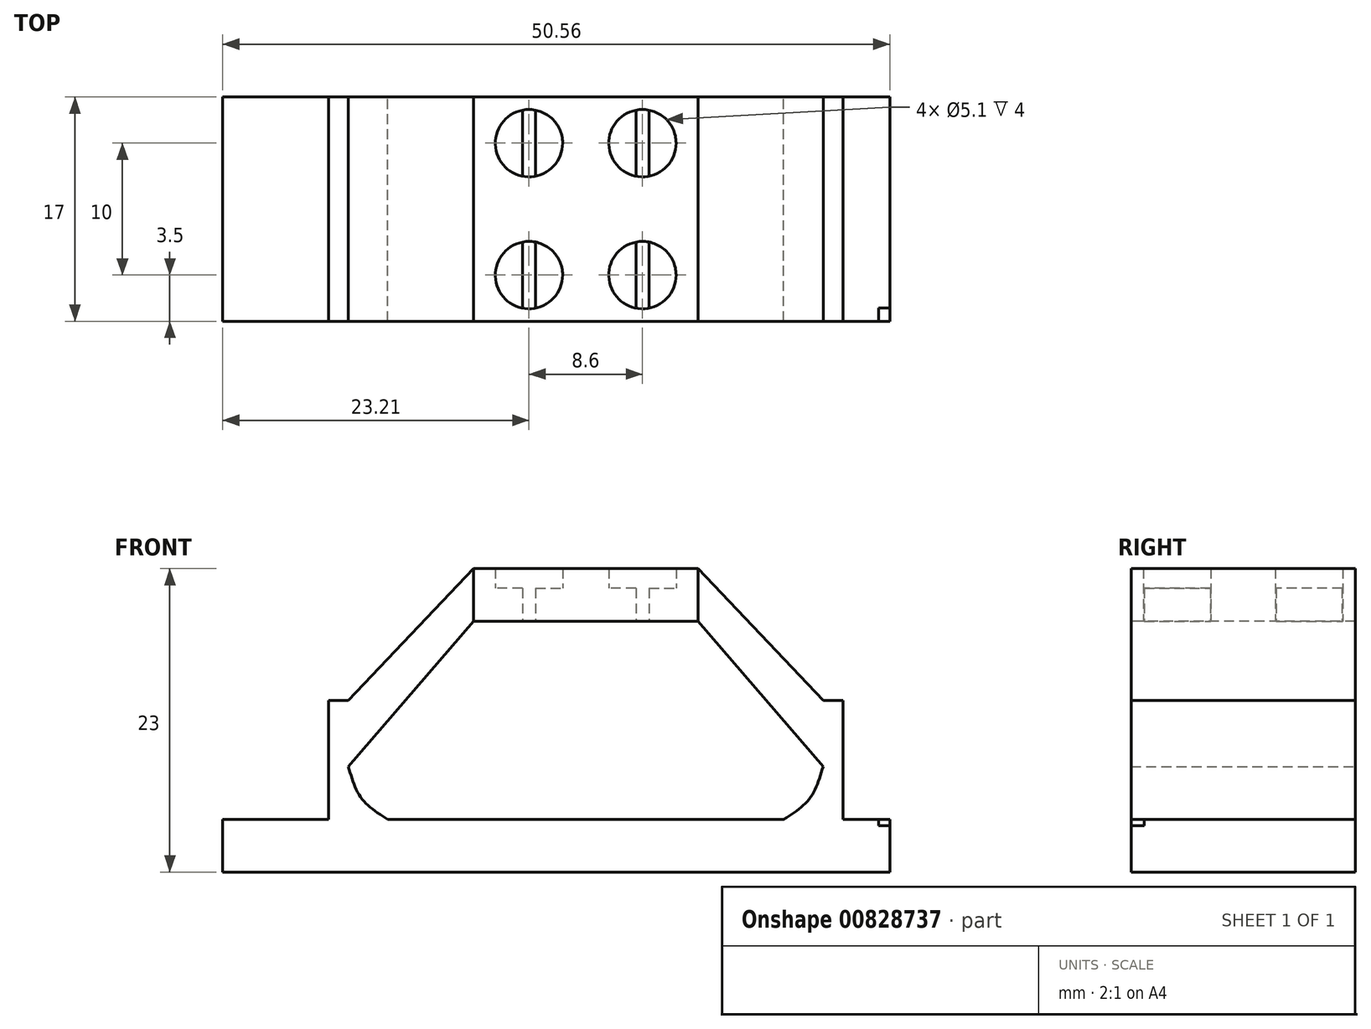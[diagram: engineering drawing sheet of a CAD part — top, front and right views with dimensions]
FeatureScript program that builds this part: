
annotation { "Feature Type Name" : "Feature", "Feature Type Description" : "" }
export const myFeature = defineFeature(function(context is Context, id is Id, definition is map)
    precondition{}
    {
        {
            assignVariable(context, id + "F0", {"name" : "Hollow", "anyValue" : 82});
        }
        {
            assignVariable(context, id + "F1", {"name" : "BaseThicknes", "anyValue" : 4});
        }
        {
            var Q0;
            Q0=qCreatedBy(makeId("Top.planeOp"),FACE);
            cPlane(context, id + "F2", {"entities" : qUnion([Q0]), "cplaneType" : CPlaneType.OFFSET, "offset" : (sqrt((sqrt((getVariable(context, 'Hollow') * getVariable(context, 'Hollow')) - ((getVariable(context, 'Hollow') / 2) * (getVariable(context, 'Hollow') / 2)))) * (sqrt((getVariable(context, 'Hollow') * getVariable(context, 'Hollow')) - ((getVariable(context, 'Hollow') / 2) * (getVariable(context, 'Hollow') / 2)))) - ((getVariable(context, 'Hollow') / 2) * (getVariable(context, 'Hollow') / 2)))) * mm, "width" : 150 * mm, "height" : 150 * mm});
        }
        {
            var Q0;
            Q0=qCreatedBy(id+"F2.planeOp",FACE);
            var sketch = newSketch(context, id + "F3", { "sketchPlane" : qUnion([Q0])});
            skPoint(sketch, "E0", {"position": v(0, 0) * mm});
            skSolve(sketch);
        }
        {
            var Q0;
            Q0=qCreatedBy(makeId("Top.planeOp"),FACE);
            var sketch = newSketch(context, id + "F4", { "sketchPlane" : qUnion([Q0])});
            skLineSegment(sketch, "E1.bottom", {"start": v(-41, 41) * mm, "end": v(41, 41) * mm});
            skLineSegment(sketch, "E1.top", {"start": v(-41, -41) * mm, "end": v(41, -41) * mm});
            skLineSegment(sketch, "E1.left", {"start": v(-41, 41) * mm, "end": v(-41, -41) * mm});
            skLineSegment(sketch, "E1.right", {"start": v(41, 41) * mm, "end": v(41, -41) * mm});
            skSolve(sketch);
        }
        {
            var Q0;
            Q0=qSketchRegion(id+"F4",true);
            extrude(context, id + "F5", {"entities" : qUnion([Q0]), "depth" : (getVariable(context, 'BaseThicknes')) * mm, "offsetDistance" : 25 * mm});
        }
        {
            var Q1;
            Q1=makeQuery(id+"F5.opExtrude","CAP_FACE",FACE,{"disambiguationData":[OSD([sQuery(id+"F4.wireOp",EDGE,"E1.bottom"),sQuery(id+"F4.wireOp",EDGE,"E1.top"),sQuery(id+"F4.wireOp",EDGE,"E1.left"),sQuery(id+"F4.wireOp",EDGE,"E1.right")])],"isStart":true});
            var Q2;
            Q2=sQuery(id+"F3.wireOp",VERTEX,"E0");
            loft(context, id + "F6", {"operationType" : NewBodyOperationType.INTERSECT, "sheetProfilesArray" : [{ "sheetProfileEntities" : qUnion([Q1]) }, { "sheetProfileEntities" : qUnion([Q2]) }]});
        }
        {
            var Q0;
            Q0=makeQuery(id+"F5.opExtrude","CAP_FACE",FACE,{"disambiguationData":[OSD([sQuery(id+"F4.wireOp",EDGE,"E1.bottom"),sQuery(id+"F4.wireOp",EDGE,"E1.top"),sQuery(id+"F4.wireOp",EDGE,"E1.left"),sQuery(id+"F4.wireOp",EDGE,"E1.right")])],"isStart":true});
            var sketch = newSketch(context, id + "F7", { "sketchPlane" : qUnion([Q0])});
            skCircle(sketch, "E2", {"center": v(-34.94, -34.94) * mm, "radius": 0.76 * mm});
            skCircle(sketch, "E3.MirrorC", {"center": v(34.94, -34.94) * mm, "radius": 0.76 * mm});
            skCircle(sketch, "E4.MirrorC", {"center": v(34.94, 34.94) * mm, "radius": 0.76 * mm});
            skCircle(sketch, "E5.MirrorC", {"center": v(-34.94, 34.94) * mm, "radius": 0.76 * mm});
            skCircle(sketch, "E6", {"center": v(-34.94, -34.94) * mm, "radius": 1.51 * mm});
            skCircle(sketch, "E7.MirrorC", {"center": v(-34.94, 34.94) * mm, "radius": 1.51 * mm});
            skCircle(sketch, "E8.MirrorC", {"center": v(34.94, -34.94) * mm, "radius": 1.51 * mm});
            skCircle(sketch, "E9.MirrorC", {"center": v(34.94, 34.94) * mm, "radius": 1.51 * mm});
            skSolve(sketch);
        }
        {
            var Q0;
            Q0=makeQuery(id+"F7.imprint","IMPRINT",FACE,{"disambiguationData":[TD([[makeQuery(id+"F7.imprint","IMPRINT",EDGE,{"derivedFrom":sQuery(id+"F7.wireOp",EDGE,"E2")}),1.0]])]});
            var Q1;
            Q1=makeQuery(id+"F7.imprint","IMPRINT",FACE,{"disambiguationData":[TD([[makeQuery(id+"F7.imprint","IMPRINT",EDGE,{"derivedFrom":sQuery(id+"F7.wireOp",EDGE,"E5.MirrorC")}),-1.0]])]});
            var Q2;
            Q2=makeQuery(id+"F7.imprint","IMPRINT",FACE,{"disambiguationData":[TD([[makeQuery(id+"F7.imprint","IMPRINT",EDGE,{"derivedFrom":sQuery(id+"F7.wireOp",EDGE,"E4.MirrorC")}),1.0]])]});
            var Q3;
            Q3=makeQuery(id+"F7.imprint","IMPRINT",FACE,{"disambiguationData":[TD([[makeQuery(id+"F7.imprint","IMPRINT",EDGE,{"derivedFrom":sQuery(id+"F7.wireOp",EDGE,"E3.MirrorC")}),-1.0]])]});
            extrude(context, id + "F8", {"entities" : qUnion([Q0, Q1, Q2, Q3]), "operationType" : NewBodyOperationType.REMOVE, "oppositeDirection" : true, "depth" : 25 * mm, "offsetDistance" : 25 * mm});
        }
        {
            var Q0;
            Q0=makeQuery(id+"F7.imprint","IMPRINT",FACE,{"disambiguationData":[TD([[makeQuery(id+"F7.imprint","IMPRINT",EDGE,{"derivedFrom":sQuery(id+"F7.wireOp",EDGE,"E5.MirrorC")}),1.0]])]});
            var Q1;
            Q1=makeQuery(id+"F7.imprint","IMPRINT",FACE,{"disambiguationData":[TD([[makeQuery(id+"F7.imprint","IMPRINT",EDGE,{"derivedFrom":sQuery(id+"F7.wireOp",EDGE,"E4.MirrorC")}),-1.0]])]});
            var Q2;
            Q2=makeQuery(id+"F7.imprint","IMPRINT",FACE,{"disambiguationData":[TD([[makeQuery(id+"F7.imprint","IMPRINT",EDGE,{"derivedFrom":sQuery(id+"F7.wireOp",EDGE,"E2")}),-1.0]])]});
            var Q3;
            Q3=makeQuery(id+"F7.imprint","IMPRINT",FACE,{"disambiguationData":[TD([[makeQuery(id+"F7.imprint","IMPRINT",EDGE,{"derivedFrom":sQuery(id+"F7.wireOp",EDGE,"E3.MirrorC")}),1.0]])]});
            extrude(context, id + "F9", {"entities" : qUnion([Q0, Q1, Q2, Q3]), "operationType" : NewBodyOperationType.REMOVE, "oppositeDirection" : true, "depth" : 2 * mm, "offsetDistance" : 25 * mm});
        }
        {
            var Q0;
            Q0=makeQuery(id+"F5.opExtrude","CAP_FACE",FACE,{"disambiguationData":[OSD([sQuery(id+"F4.wireOp",EDGE,"E1.bottom"),sQuery(id+"F4.wireOp",EDGE,"E1.top"),sQuery(id+"F4.wireOp",EDGE,"E1.left"),sQuery(id+"F4.wireOp",EDGE,"E1.right")])],"isStart":false});
            var sketch = newSketch(context, id + "F10", { "sketchPlane" : qUnion([Q0])});
            skLineSegment(sketch, "E10.bottom", {"start": v(-30, 29.5) * mm, "end": v(-26.3, 29.5) * mm});
            skLineSegment(sketch, "E10.top", {"start": v(-30, -16.5) * mm, "end": v(-26.3, -16.5) * mm});
            skLineSegment(sketch, "E10.left", {"start": v(-30, 29.5) * mm, "end": v(-30, -16.5) * mm});
            skLineSegment(sketch, "E10.right", {"start": v(-19.5, 29.5) * mm, "end": v(-19.5, -16.5) * mm});
            skLineSegment(sketch, "E11.bottom", {"start": v(-31.5, 31.5) * mm, "end": v(-26.3, 31.5) * mm});
            skLineSegment(sketch, "E11.top", {"start": v(-31.5, -18.5) * mm, "end": v(-18, -18.5) * mm});
            skLineSegment(sketch, "E11.left", {"start": v(-31.5, 31.5) * mm, "end": v(-31.5, -18.5) * mm});
            skLineSegment(sketch, "E11.right", {"start": v(-18, 31.5) * mm, "end": v(-18, -18.5) * mm});
            skLineSegment(sketch, "E12", {"start": v(-30, 27.7) * mm, "end": v(-28, 27.7) * mm});
            skLineSegment(sketch, "E13", {"start": v(-30, 28.7) * mm, "end": v(-28, 28.7) * mm});
            skLineSegment(sketch, "E14.left", {"start": v(-21.5, 28.7) * mm, "end": v(-21.5, 27.7) * mm});
            skLineSegment(sketch, "E14.right", {"start": v(-28, 28.7) * mm, "end": v(-28, 27.7) * mm});
            skLineSegment(sketch, "E15", {"start": v(-18, 6.5) * mm, "end": v(-31.5, 6.5) * mm, "construction": true});
            skLineSegment(sketch, "E16.trimOffspring", {"start": v(-21.5, 27.7) * mm, "end": v(-19.5, 27.7) * mm});
            skLineSegment(sketch, "E17.trimOffspring", {"start": v(-21.5, 28.7) * mm, "end": v(-19.5, 28.7) * mm});
            skLineSegment(sketch, "E18.MirrorCS", {"start": v(-30, -15.7) * mm, "end": v(-28, -15.7) * mm});
            skLineSegment(sketch, "E19.MirrorCS", {"start": v(-30, -14.7) * mm, "end": v(-28, -14.7) * mm});
            skLineSegment(sketch, "E20.MirrorCS", {"start": v(-21.5, -15.7) * mm, "end": v(-21.5, -14.7) * mm});
            skLineSegment(sketch, "E21.MirrorCS", {"start": v(-21.5, -15.7) * mm, "end": v(-19.5, -15.7) * mm});
            skLineSegment(sketch, "E22.MirrorCS", {"start": v(-21.5, -14.7) * mm, "end": v(-19.5, -14.7) * mm});
            skLineSegment(sketch, "E23.MirrorCS", {"start": v(-28, -15.7) * mm, "end": v(-28, -14.7) * mm});
            skLineSegment(sketch, "E24", {"start": v(-26.3, 31.5) * mm, "end": v(-26.3, 29.5) * mm});
            skLineSegment(sketch, "E25", {"start": v(-23.2, 31.5) * mm, "end": v(-23.2, 29.5) * mm});
            skLineSegment(sketch, "E26.trimOffspring", {"start": v(-23.2, 31.5) * mm, "end": v(-18, 31.5) * mm});
            skLineSegment(sketch, "E27.trimOffspring", {"start": v(-23.2, 29.5) * mm, "end": v(-19.5, 29.5) * mm});
            skLineSegment(sketch, "E28.MirrorCS", {"start": v(-26.3, -18.5) * mm, "end": v(-26.3, -16.5) * mm});
            skLineSegment(sketch, "E29.MirrorCS", {"start": v(-23.2, -18.5) * mm, "end": v(-23.2, -16.5) * mm});
            skLineSegment(sketch, "E30.trimOffspring", {"start": v(-23.2, -16.5) * mm, "end": v(-19.5, -16.5) * mm});
            skLineSegment(sketch, "E31.MirrorCS", {"start": v(21.5, 28.7) * mm, "end": v(21.5, 27.7) * mm});
            skLineSegment(sketch, "E32.MirrorCS", {"start": v(21.5, 28.7) * mm, "end": v(19.5, 28.7) * mm});
            skLineSegment(sketch, "E33.MirrorCS", {"start": v(23.2, 29.5) * mm, "end": v(19.5, 29.5) * mm});
            skLineSegment(sketch, "E34.MirrorCS", {"start": v(23.2, 31.5) * mm, "end": v(23.2, 29.5) * mm});
            skLineSegment(sketch, "E35.MirrorCS", {"start": v(28, -15.7) * mm, "end": v(28, -14.7) * mm});
            skLineSegment(sketch, "E36.MirrorCS", {"start": v(21.5, -15.7) * mm, "end": v(19.5, -15.7) * mm});
            skLineSegment(sketch, "E37.MirrorCS", {"start": v(23.2, -16.5) * mm, "end": v(19.5, -16.5) * mm});
            skLineSegment(sketch, "E38.MirrorCS", {"start": v(30, -15.7) * mm, "end": v(28, -15.7) * mm});
            skLineSegment(sketch, "E39.MirrorCS", {"start": v(21.5, -14.7) * mm, "end": v(19.5, -14.7) * mm});
            skLineSegment(sketch, "E40.MirrorCS", {"start": v(30, 29.5) * mm, "end": v(26.3, 29.5) * mm});
            skLineSegment(sketch, "E41.MirrorCS", {"start": v(30, 28.7) * mm, "end": v(28, 28.7) * mm});
            skLineSegment(sketch, "E42.MirrorCS", {"start": v(30, -16.5) * mm, "end": v(26.3, -16.5) * mm});
            skLineSegment(sketch, "E43.MirrorCS", {"start": v(26.3, 31.5) * mm, "end": v(26.3, 29.5) * mm});
            skLineSegment(sketch, "E44.MirrorCS", {"start": v(21.5, -15.7) * mm, "end": v(21.5, -14.7) * mm});
            skLineSegment(sketch, "E45.MirrorCS", {"start": v(28, 28.7) * mm, "end": v(28, 27.7) * mm});
            skLineSegment(sketch, "E46.MirrorCS", {"start": v(30, -14.7) * mm, "end": v(28, -14.7) * mm});
            skLineSegment(sketch, "E47.MirrorCS", {"start": v(31.5, 31.5) * mm, "end": v(26.3, 31.5) * mm});
            skLineSegment(sketch, "E48.MirrorCS", {"start": v(21.5, 27.7) * mm, "end": v(19.5, 27.7) * mm});
            skLineSegment(sketch, "E49.MirrorCS", {"start": v(23.2, -18.5) * mm, "end": v(23.2, -16.5) * mm});
            skLineSegment(sketch, "E50.MirrorCS", {"start": v(30, 27.7) * mm, "end": v(28, 27.7) * mm});
            skLineSegment(sketch, "E51.MirrorCS", {"start": v(26.3, -18.5) * mm, "end": v(26.3, -16.5) * mm});
            skLineSegment(sketch, "E52.MirrorCS", {"start": v(23.2, 31.5) * mm, "end": v(18, 31.5) * mm});
            skLineSegment(sketch, "E53.MirrorCS", {"start": v(31.5, 31.5) * mm, "end": v(31.5, -18.5) * mm});
            skLineSegment(sketch, "E54.MirrorCS", {"start": v(30, 29.5) * mm, "end": v(30, -16.5) * mm});
            skLineSegment(sketch, "E55.MirrorCS", {"start": v(31.5, -18.5) * mm, "end": v(18, -18.5) * mm});
            skLineSegment(sketch, "E56.MirrorCS", {"start": v(19.5, 29.5) * mm, "end": v(19.5, -16.5) * mm});
            skLineSegment(sketch, "E57.MirrorCS", {"start": v(18, 31.5) * mm, "end": v(18, -18.5) * mm});
            skLineSegment(sketch, "E58.MirrorCS", {"start": v(18, 6.5) * mm, "end": v(31.5, 6.5) * mm, "construction": true});
            skSolve(sketch);
        }
        {
            var Q0;
            {var subQ5=sQuery(id+"F10.wireOp",EDGE,"E33.MirrorCS");Q0=makeQuery(id+"F10.imprint","IMPRINT",FACE,{"disambiguationData":[TD([[makeQuery(id+"F10.imprint","IMPRINT",EDGE,{"derivedFrom":subQ5}),-1.0]])]});}
            var Q1;
            {var subQ6=sQuery(id+"F10.wireOp",EDGE,"E40.MirrorCS");Q1=makeQuery(id+"F10.imprint","IMPRINT",FACE,{"disambiguationData":[TD([[makeQuery(id+"F10.imprint","IMPRINT",EDGE,{"derivedFrom":subQ6}),-1.0]])]});}
            var Q2;
            Q2=makeQuery(id+"F10.imprint","IMPRINT",FACE,{"disambiguationData":[TD([[makeQuery(id+"F10.imprint","IMPRINT",EDGE,{"derivedFrom":sQuery(id+"F10.wireOp",EDGE,"E31.MirrorCS")}),-1.0]])]});
            var Q3;
            {var subQ0=sQuery(id+"F10.wireOp",EDGE,"E41.MirrorCS");Q3=makeQuery(id+"F10.imprint","IMPRINT",FACE,{"disambiguationData":[TD([[makeQuery(id+"F10.imprint","IMPRINT",EDGE,{"derivedFrom":subQ0}),1.0]])]});}
            var Q4;
            {var subQ0=sQuery(id+"F10.wireOp",EDGE,"E36.MirrorCS");Q4=makeQuery(id+"F10.imprint","IMPRINT",FACE,{"disambiguationData":[TD([[makeQuery(id+"F10.imprint","IMPRINT",EDGE,{"derivedFrom":subQ0}),-1.0]])]});}
            var Q5;
            Q5=makeQuery(id+"F10.imprint","IMPRINT",FACE,{"disambiguationData":[TD([[makeQuery(id+"F10.imprint","IMPRINT",EDGE,{"derivedFrom":sQuery(id+"F10.wireOp",EDGE,"E35.MirrorCS")}),-1.0]])]});
            var Q6;
            Q6=makeQuery(id+"F10.imprint","IMPRINT",FACE,{"disambiguationData":[TD([[makeQuery(id+"F10.imprint","IMPRINT",EDGE,{"derivedFrom":sQuery(id+"F10.wireOp",EDGE,"E20.MirrorCS")}),-1.0]])]});
            var Q7;
            {var subQ0=sQuery(id+"F10.wireOp",EDGE,"E18.MirrorCS");Q7=makeQuery(id+"F10.imprint","IMPRINT",FACE,{"disambiguationData":[TD([[makeQuery(id+"F10.imprint","IMPRINT",EDGE,{"derivedFrom":subQ0}),1.0]])]});}
            var Q8;
            {var subQ6=sQuery(id+"F10.wireOp",EDGE,"E10.bottom");Q8=makeQuery(id+"F10.imprint","IMPRINT",FACE,{"disambiguationData":[TD([[makeQuery(id+"F10.imprint","IMPRINT",EDGE,{"derivedFrom":subQ6}),1.0]])]});}
            var Q9;
            {var subQ0=sQuery(id+"F10.wireOp",EDGE,"E11.right");Q9=makeQuery(id+"F10.imprint","IMPRINT",FACE,{"disambiguationData":[TD([[makeQuery(id+"F10.imprint","IMPRINT",EDGE,{"derivedFrom":subQ0}),-1.0]])]});}
            var Q10;
            {var subQ0=sQuery(id+"F10.wireOp",EDGE,"E12");Q10=makeQuery(id+"F10.imprint","IMPRINT",FACE,{"disambiguationData":[TD([[makeQuery(id+"F10.imprint","IMPRINT",EDGE,{"derivedFrom":subQ0}),1.0]])]});}
            var Q11;
            Q11=makeQuery(id+"F10.imprint","IMPRINT",FACE,{"disambiguationData":[TD([[makeQuery(id+"F10.imprint","IMPRINT",EDGE,{"derivedFrom":sQuery(id+"F10.wireOp",EDGE,"E14.left")}),1.0]])]});
            extrude(context, id + "F11", {"entities" : qUnion([Q0, Q1, Q2, Q3, Q4, Q5, Q6, Q7, Q8, Q9, Q10, Q11]), "operationType" : NewBodyOperationType.ADD, "depth" : 9 * mm, "offsetDistance" : 25 * mm});
        }
        {
            var Q0;
            Q0=qCreatedBy(makeId("Front.planeOp"),FACE);
            var sketch = newSketch(context, id + "F12", { "sketchPlane" : qUnion([Q0])});
            skLineSegment(sketch, "E59", {"start": v(-31.5, 4) * mm, "end": v(-34.5, 4) * mm});
            skLineSegment(sketch, "E60", {"start": v(-31.5, 4) * mm, "end": v(-31.5, 8) * mm});
            skPoint(sketch, "E61", {"position": v(-34.5, 4) * mm});
            skFitSpline(sketch, "E62", {"points": [v(-31.5, 8) * mm, v(-32.5, 5.6) * mm, v(-34.5, 4) * mm], "startDerivative": vector(-1.67, -5.36) * mm, "endDerivative": vector(-4.69, -2.88) * mm});
            skLineSegment(sketch, "E63", {"start": v(-24.75, 13.95) * mm, "end": v(-24.75, 2.35) * mm, "construction": true});
            skFitSpline(sketch, "E64.MirrorCS", {"points": [v(-18, 8) * mm, v(-17, 5.6) * mm, v(-15, 4) * mm], "startDerivative": vector(1.67, -5.36) * mm, "endDerivative": vector(4.69, -2.88) * mm});
            skFitSpline(sketch, "E65.MirrorCS", {"points": [v(18, 8) * mm, v(17, 5.6) * mm, v(15, 4) * mm], "startDerivative": vector(-1.67, -5.36) * mm, "endDerivative": vector(-4.69, -2.88) * mm});
            skFitSpline(sketch, "E66.MirrorCS", {"points": [v(31.5, 8) * mm, v(32.5, 5.6) * mm, v(34.5, 4) * mm], "startDerivative": vector(1.67, -5.36) * mm, "endDerivative": vector(4.69, -2.88) * mm});
            skLineSegment(sketch, "E67.MirrorCS", {"start": v(-18, 4) * mm, "end": v(-15, 4) * mm});
            skLineSegment(sketch, "E68.MirrorCS", {"start": v(18, 4) * mm, "end": v(15, 4) * mm});
            skLineSegment(sketch, "E69.MirrorCS", {"start": v(31.5, 4) * mm, "end": v(34.5, 4) * mm});
            skLineSegment(sketch, "E70.MirrorCS", {"start": v(-18, 4) * mm, "end": v(-18, 8) * mm});
            skLineSegment(sketch, "E71.MirrorCS", {"start": v(18, 4) * mm, "end": v(18, 8) * mm});
            skLineSegment(sketch, "E72.MirrorCS", {"start": v(31.5, 4) * mm, "end": v(31.5, 8) * mm});
            skSolve(sketch);
        }
        {
            var Q0;
            Q0=qSketchRegion(id+"F12",true);
            extrude(context, id + "F13", {"entities" : qUnion([Q0]), "operationType" : NewBodyOperationType.ADD, "depth" : 18.5 * mm, "offsetDistance" : 25 * mm, "hasSecondDirection" : true, "secondDirectionOppositeDirection" : true, "secondDirectionDepth" : 31.5 * mm});
        }
        {
            var Q0;
            Q0=qCreatedBy(makeId("Right.planeOp"),FACE);
            var sketch = newSketch(context, id + "F14", { "sketchPlane" : qUnion([Q0])});
            skCircle(sketch, "E73", {"center": v(17.5, 13) * mm, "radius": 9 * mm});
            skCircle(sketch, "E74", {"center": v(-3.5, 13) * mm, "radius": 9 * mm});
            skSolve(sketch);
        }
        {
            var Q0;
            Q0=makeQuery(id+"F14.imprint","IMPRINT",FACE,{"disambiguationData":[TD([[makeQuery(id+"F14.imprint","IMPRINT",EDGE,{"derivedFrom":sQuery(id+"F14.wireOp",EDGE,"E73")}),1.0]])]});
            extrude(context, id + "F15", {"entities" : qUnion([Q0]), "operationType" : NewBodyOperationType.REMOVE, "oppositeDirection" : true, "depth" : 50 * mm, "offsetDistance" : 25 * mm, "hasSecondDirection" : true, "secondDirectionOppositeDirection" : false, "secondDirectionDepth" : 52.3 * mm});
        }
        {
            var Q0;
            Q0=makeQuery(id+"F5.opExtrude","CAP_FACE",FACE,{"disambiguationData":[OSD([sQuery(id+"F4.wireOp",EDGE,"E1.bottom"),sQuery(id+"F4.wireOp",EDGE,"E1.top"),sQuery(id+"F4.wireOp",EDGE,"E1.left"),sQuery(id+"F4.wireOp",EDGE,"E1.right")])],"isStart":false});
            var sketch = newSketch(context, id + "F16", { "sketchPlane" : qUnion([Q0])});
            skLineSegment(sketch, "E75.bottom", {"start": v(-7.5, -21.5) * mm, "end": v(7.5, -21.5) * mm});
            skLineSegment(sketch, "E75.top", {"start": v(-7.5, -31.5) * mm, "end": v(7.5, -31.5) * mm});
            skLineSegment(sketch, "E75.left", {"start": v(-7.5, -21.5) * mm, "end": v(-7.5, -31.5) * mm});
            skLineSegment(sketch, "E75.right", {"start": v(7.5, -21.5) * mm, "end": v(7.5, -31.5) * mm});
            skSolve(sketch);
        }
        {
            var Q0;
            Q0=qSketchRegion(id+"F16",true);
            extrude(context, id + "F17", {"entities" : qUnion([Q0]), "operationType" : NewBodyOperationType.REMOVE, "oppositeDirection" : true, "depth" : 25 * mm, "offsetDistance" : 25 * mm});
        }
        {
            var Q0;
            Q0=makeQuery(id+"F5.opExtrude","CAP_FACE",FACE,{"disambiguationData":[OSD([sQuery(id+"F4.wireOp",EDGE,"E1.bottom"),sQuery(id+"F4.wireOp",EDGE,"E1.top"),sQuery(id+"F4.wireOp",EDGE,"E1.left"),sQuery(id+"F4.wireOp",EDGE,"E1.right")])],"isStart":true});
            var sketch = newSketch(context, id + "F18", { "sketchPlane" : qUnion([Q0])});
            skLineSegment(sketch, "E76.bottom", {"start": v(-9.5, 33.5) * mm, "end": v(9.5, 33.5) * mm});
            skLineSegment(sketch, "E76.top", {"start": v(-9.5, 19.5) * mm, "end": v(9.5, 19.5) * mm});
            skLineSegment(sketch, "E76.left", {"start": v(-9.5, 33.5) * mm, "end": v(-9.5, 19.5) * mm});
            skLineSegment(sketch, "E76.right", {"start": v(9.5, 33.5) * mm, "end": v(9.5, 19.5) * mm});
            skSolve(sketch);
        }
        {
            var Q0;
            Q0=qSketchRegion(id+"F18",true);
            extrude(context, id + "F19", {"entities" : qUnion([Q0]), "operationType" : NewBodyOperationType.REMOVE, "oppositeDirection" : true, "depth" : 2 * mm, "offsetDistance" : 25 * mm});
        }
        {
            var Q0;
            Q0=makeQuery(id+"F5.opExtrude","CAP_FACE",FACE,{"disambiguationData":[OSD([sQuery(id+"F4.wireOp",EDGE,"E1.bottom"),sQuery(id+"F4.wireOp",EDGE,"E1.top"),sQuery(id+"F4.wireOp",EDGE,"E1.left"),sQuery(id+"F4.wireOp",EDGE,"E1.right")])],"isStart":false});
            var sketch = newSketch(context, id + "F20", { "sketchPlane" : qUnion([Q0])});
            skLineSegment(sketch, "E77.bottom", {"start": v(-25.25, 23.5) * mm, "end": v(-24.25, 23.5) * mm});
            skLineSegment(sketch, "E77.top", {"start": v(-25.25, 18.5) * mm, "end": v(-24.25, 18.5) * mm});
            skLineSegment(sketch, "E77.left", {"start": v(-25.25, 23.5) * mm, "end": v(-25.25, 18.5) * mm});
            skLineSegment(sketch, "E77.right", {"start": v(-24.25, 23.5) * mm, "end": v(-24.25, 18.5) * mm});
            skLineSegment(sketch, "E78.bottom", {"start": v(-27.25, 21.5) * mm, "end": v(-22.25, 21.5) * mm});
            skLineSegment(sketch, "E78.top", {"start": v(-27.25, 20.5) * mm, "end": v(-22.25, 20.5) * mm});
            skLineSegment(sketch, "E78.left", {"start": v(-27.25, 21.5) * mm, "end": v(-27.25, 20.5) * mm});
            skLineSegment(sketch, "E78.right", {"start": v(-22.25, 21.5) * mm, "end": v(-22.25, 20.5) * mm});
            skLineSegment(sketch, "E79", {"start": v(-24.75, 32.18) * mm, "end": v(-24.75, -20.77) * mm, "construction": true});
            skLineSegment(sketch, "E80.bottom", {"start": v(24.2, -5.5) * mm, "end": v(25.2, -5.5) * mm});
            skLineSegment(sketch, "E80.top", {"start": v(24.2, -10.5) * mm, "end": v(25.2, -10.5) * mm});
            skLineSegment(sketch, "E80.left", {"start": v(24.2, -5.5) * mm, "end": v(24.2, -10.5) * mm});
            skLineSegment(sketch, "E80.right", {"start": v(25.2, -5.5) * mm, "end": v(25.2, -10.5) * mm});
            skLineSegment(sketch, "E81.bottom", {"start": v(22.2, -7.5) * mm, "end": v(27.2, -7.5) * mm});
            skLineSegment(sketch, "E81.top", {"start": v(22.2, -8.5) * mm, "end": v(27.2, -8.5) * mm});
            skLineSegment(sketch, "E81.left", {"start": v(22.2, -7.5) * mm, "end": v(22.2, -8.5) * mm});
            skLineSegment(sketch, "E81.right", {"start": v(27.2, -7.5) * mm, "end": v(27.2, -8.5) * mm});
            skLineSegment(sketch, "E82", {"start": v(24.7, 5.1) * mm, "end": v(24.7, -19.14) * mm, "construction": true});
            skText(sketch, "E83", { "text": "PW SW", "fontName": "OpenSans-Regular.ttf"});
            const initialGuessF20  = {"E83": [-0.00532, -0.01924, 1, 0, 0.00251]};
            skSetInitialGuess(sketch, initialGuessF20);
            skSolve(sketch);
        }
        {
            var Q0;
            Q0=qSketchRegion(id+"F20",true);
            extrude(context, id + "F21", {"entities" : qUnion([Q0]), "operationType" : NewBodyOperationType.REMOVE, "oppositeDirection" : true, "depth" : .5 * mm, "offsetDistance" : 25 * mm});
        }
        {
            var Q0;
            Q0=makeQuery(id+"F20.imprint","IMPRINT",FACE,{"disambiguationData":[TD([[makeQuery(id+"F20.imprint","IMPRINT",EDGE,{"derivedFrom":sQuery(id+"F20.wireOp",EDGE,"E83.sketch_text.stroke-35")}),-1.0]])]});
            var Q1;
            Q1=makeQuery(id+"F20.imprint","IMPRINT",FACE,{"disambiguationData":[TD([[makeQuery(id+"F20.imprint","IMPRINT",EDGE,{"derivedFrom":sQuery(id+"F20.wireOp",EDGE,"E83.sketch_text.stroke-60")}),-1.0]])]});
            var Q2;
            Q2=makeQuery(id+"F20.imprint","IMPRINT",FACE,{"disambiguationData":[TD([[makeQuery(id+"F20.imprint","IMPRINT",EDGE,{"derivedFrom":sQuery(id+"F20.wireOp",EDGE,"E83.sketch_text.stroke-15")}),-1.0]])]});
            var Q3;
            Q3=makeQuery(id+"F20.imprint","IMPRINT",FACE,{"disambiguationData":[TD([[makeQuery(id+"F20.imprint","IMPRINT",EDGE,{"derivedFrom":sQuery(id+"F20.wireOp",EDGE,"E83.sketch_text.stroke-0")}),-1.0]])]});
            extrude(context, id + "F22", {"entities" : qUnion([Q0, Q1, Q2, Q3]), "operationType" : NewBodyOperationType.REMOVE, "oppositeDirection" : true, "depth" : .5 * mm, "offsetDistance" : 25 * mm});
        }
        {
            var Q0;
            {var subQ15=sQuery(id+"F4.wireOp",EDGE,"E1.right");var subQ16=sQuery(id+"F4.wireOp",EDGE,"E1.left");var subQ17=sQuery(id+"F4.wireOp",EDGE,"E1.top");var subQ18=sQuery(id+"F4.wireOp",EDGE,"E1.bottom");var subQ19=makeQuery(id+"F5.opExtrude","CAP_FACE",FACE,{"disambiguationData":[OSD([subQ18,subQ17,subQ16,subQ15])],"isStart":false});Q0=makeQuery(id+"F21.boolean.opBoolean","SPLIT",FACE,{"disambiguationData":[TD([makeQuery(id+"F8.boolean.opBoolean","COPY",FACE,{"derivedFrom":makeQuery(id+"F8.opExtrude","SWEPT_FACE",FACE,{"disambiguationData":[OSD([sQuery(id+"F7.wireOp",EDGE,"E2")])]})})])],"derivedFrom":subQ19});}
            cPlane(context, id + "F23", {"entities" : qUnion([Q0]), "cplaneType" : CPlaneType.OFFSET, "offset" : 15 * mm, "width" : 150 * mm, "height" : 150 * mm});
        }
        {
            var Q0;
            Q0=qCreatedBy(id+"F23.planeOp",FACE);
            var sketch = newSketch(context, id + "F24", { "sketchPlane" : qUnion([Q0])});
            skLineSegment(sketch, "E84.bottom", {"start": v(-8.5, 8.5) * mm, "end": v(-4.8, 8.5) * mm});
            skLineSegment(sketch, "E84.top", {"start": v(-8.5, -8.5) * mm, "end": v(8.5, -8.5) * mm});
            skLineSegment(sketch, "E84.left", {"start": v(-8.5, 8.5) * mm, "end": v(-8.5, -8.5) * mm});
            skLineSegment(sketch, "E84.right", {"start": v(8.5, 8.5) * mm, "end": v(8.5, -8.5) * mm});
            skLineSegment(sketch, "E85.left", {"start": v(-4.8, 7.5) * mm, "end": v(-4.8, 2.5) * mm});
            skLineSegment(sketch, "E85.right", {"start": v(-3.8, 7.5) * mm, "end": v(-3.8, 2.5) * mm});
            skLineSegment(sketch, "E86.trimOffspring", {"start": v(-3.8, 8.5) * mm, "end": v(8.5, 8.5) * mm});
            skLineSegment(sketch, "E87.MirrorCS", {"start": v(3.8, 7.5) * mm, "end": v(3.8, 2.5) * mm});
            skLineSegment(sketch, "E88.MirrorCS", {"start": v(4.8, -7.5) * mm, "end": v(4.8, -2.5) * mm});
            skLineSegment(sketch, "E89.MirrorCS", {"start": v(3.8, -7.5) * mm, "end": v(3.8, -2.5) * mm});
            skLineSegment(sketch, "E90.MirrorCS", {"start": v(-4.8, -7.5) * mm, "end": v(-4.8, -2.5) * mm});
            skLineSegment(sketch, "E91.MirrorCS", {"start": v(-3.8, -7.5) * mm, "end": v(-3.8, -2.5) * mm});
            skCircle(sketch, "E92", {"center": v(-4.3, 5) * mm, "radius": 2.55 * mm});
            skCircle(sketch, "E93", {"center": v(4.3, 5) * mm, "radius": 2.55 * mm});
            skCircle(sketch, "E94", {"center": v(-4.3, -5) * mm, "radius": 2.55 * mm});
            skCircle(sketch, "E95", {"center": v(4.3, -5) * mm, "radius": 2.55 * mm});
            skLineSegment(sketch, "E96", {"start": v(-4.8, 8.5) * mm, "end": v(-3.8, 8.5) * mm});
            skPoint(sketch, "E97.orphan", {"position": v(3.8, 8.5) * mm});
            skPoint(sketch, "E98.orphan", {"position": v(4.8, 8.5) * mm});
            skPoint(sketch, "E99.MirrorCS.end.orphan", {"position": v(4.8, 2.5) * mm});
            skPoint(sketch, "E100.orphan", {"position": v(-4.8, -8.5) * mm});
            skPoint(sketch, "E101.orphan", {"position": v(-3.8, -8.5) * mm});
            skPoint(sketch, "E102.orphan", {"position": v(3.8, -8.5) * mm});
            skPoint(sketch, "E103.orphan", {"position": v(4.8, -8.5) * mm});
            skLineSegment(sketch, "E104", {"start": v(4.8, 2.5) * mm, "end": v(4.8, 7.5) * mm});
            skSolve(sketch);
        }
        {
            var Q0;
            Q0=makeQuery(id+"F24.imprint","IMPRINT",FACE,{"disambiguationData":[TD([[makeQuery(id+"F24.imprint","IMPRINT",EDGE,{"derivedFrom":sQuery(id+"F24.wireOp",EDGE,"E84.bottom")}),-1.0]])]});
            extrude(context, id + "F25", {"entities" : qUnion([Q0]), "depth" : 4 * mm, "offsetDistance" : 25 * mm});
        }
        {
            var Q0;
            {var subQ1=sQuery(id+"F10.wireOp",EDGE,"E11.right");var subQ2=sQuery(id+"F10.wireOp",EDGE,"E11.top");Q0=makeQuery(id+"F15.boolean.opBoolean","SPLIT",FACE,{"disambiguationData":[TD([makeQuery(id+"F11.opExtrude","SWEPT_FACE",FACE,{"disambiguationData":[OSD([subQ2]),TDD([makeQuery(id+"F10.imprint","IMPRINT",EDGE,{"disambiguationData":[TD([[makeQuery(id+"F10.imprint","INTERSECT",VERTEX,{"derivedFrom":[subQ2,subQ1]}),1.0]])],"derivedFrom":subQ2})])]})])],"derivedFrom":makeQuery(id+"F11.opExtrude","SWEPT_FACE",FACE,{"disambiguationData":[OSD([subQ1])]})});}
            var Q1;
            Q1=makeQuery(id+"F25.opExtrude","SWEPT_FACE",FACE,{"disambiguationData":[OSD([sQuery(id+"F24.wireOp",EDGE,"E84.left")])]});
            loft(context, id + "F26", {"sheetProfilesArray" : [{ "sheetProfileEntities" : qUnion([Q0]) }, { "sheetProfileEntities" : qUnion([Q1]) }]});
        }
        {
            var Q0;
            {var subQ1=sQuery(id+"F10.wireOp",EDGE,"E55.MirrorCS");var subQ2=sQuery(id+"F10.wireOp",EDGE,"E49.MirrorCS");var subQ3=sQuery(id+"F10.wireOp",EDGE,"E57.MirrorCS");Q0=makeQuery(id+"F15.boolean.opBoolean","SPLIT",FACE,{"disambiguationData":[TD([makeQuery(id+"F11.opExtrude","SWEPT_FACE",FACE,{"disambiguationData":[OSD([subQ1]),TDD([makeQuery(id+"F10.imprint","IMPRINT",EDGE,{"disambiguationData":[TD([[makeQuery(id+"F10.imprint","INTERSECT",VERTEX,{"derivedFrom":[subQ2,subQ1]}),-1.0]])],"derivedFrom":subQ1})])]})])],"derivedFrom":makeQuery(id+"F11.opExtrude","SWEPT_FACE",FACE,{"disambiguationData":[OSD([subQ3])]})});}
            var Q1;
            Q1=makeQuery(id+"F25.opExtrude","SWEPT_FACE",FACE,{"disambiguationData":[OSD([sQuery(id+"F24.wireOp",EDGE,"E84.right")])]});
            loft(context, id + "F27", {"sheetProfilesArray" : [{ "sheetProfileEntities" : qUnion([Q0]) }, { "sheetProfileEntities" : qUnion([Q1]) }]});
        }
        {
            var Q0;
            {var subQ0=sQuery(id+"F10.wireOp",EDGE,"E30.trimOffspring");var subQ1=sQuery(id+"F10.wireOp",EDGE,"E29.MirrorCS");var subQ2=sQuery(id+"F10.wireOp",EDGE,"E10.right");var subQ3=sQuery(id+"F10.wireOp",EDGE,"E21.MirrorCS");var subQ4=sQuery(id+"F10.wireOp",EDGE,"E16.trimOffspring");var subQ5=sQuery(id+"F10.wireOp",EDGE,"E22.MirrorCS");var subQ6=sQuery(id+"F10.wireOp",EDGE,"E11.right");var subQ7=sQuery(id+"F10.wireOp",EDGE,"E20.MirrorCS");var subQ8=sQuery(id+"F10.wireOp",EDGE,"E11.top");Q0=makeQuery(id+"F15.boolean.opBoolean","SPLIT",FACE,{"disambiguationData":[TD([makeQuery(id+"F11.opExtrude","SWEPT_FACE",FACE,{"disambiguationData":[OSD([subQ7])]})])],"derivedFrom":makeQuery(id+"F11.opExtrude","CAP_FACE",FACE,{"disambiguationData":[OSD([subQ2,subQ8,subQ6,sQuery(id+"F10.wireOp",EDGE,"E14.left"),subQ4,sQuery(id+"F10.wireOp",EDGE,"E17.trimOffspring"),subQ7,subQ3,subQ5,sQuery(id+"F10.wireOp",EDGE,"E25"),sQuery(id+"F10.wireOp",EDGE,"E26.trimOffspring"),sQuery(id+"F10.wireOp",EDGE,"E27.trimOffspring"),subQ1,subQ0])],"isStart":false})});}
            var sketch = newSketch(context, id + "F28", { "sketchPlane" : qUnion([Q0])});
            skLineSegment(sketch, "E105", {"start": v(-19.5, 5) * mm, "end": v(-19.5, -5) * mm});
            skLineSegment(sketch, "E106", {"start": v(-19.5, -5) * mm, "end": v(-18, -3.5) * mm});
            skLineSegment(sketch, "E107", {"start": v(-18, -3.5) * mm, "end": v(-18, 3.5) * mm});
            skLineSegment(sketch, "E108", {"start": v(-18, 3.5) * mm, "end": v(-19.5, 5) * mm});
            skLineSegment(sketch, "E109.MirrorCS", {"start": v(18, 3.5) * mm, "end": v(19.5, 5) * mm});
            skLineSegment(sketch, "E110.MirrorCS", {"start": v(19.5, -5) * mm, "end": v(18, -3.5) * mm});
            skLineSegment(sketch, "E111.MirrorCS", {"start": v(19.5, 5) * mm, "end": v(19.5, -5) * mm});
            skLineSegment(sketch, "E112.MirrorCS", {"start": v(18, -3.5) * mm, "end": v(18, 3.5) * mm});
            skSolve(sketch);
        }
        {
            var Q0;
            Q0 = qSketchRegion(id + "F28", true);
            extrude(context, id + "F29", {"entities" : qUnion([Q0]), "operationType" : NewBodyOperationType.REMOVE, "oppositeDirection" : true, "depth" : 4 * mm, "offsetDistance" : 25 * mm});
        }
        {
            var Q0;
            Q0 = qSketchRegion(id + "F28", true);
            extrude(context, id + "F30", {"entities" : qUnion([Q0]), "operationType" : NewBodyOperationType.ADD, "depth" : -4 * mm, "offsetDistance" : 25 * mm});
        }
        {
            var Q0;
            Q0=makeQuery(id+"F25.opExtrude","CAP_FACE",FACE,{"disambiguationData":[OSD([sQuery(id+"F24.wireOp",EDGE,"E84.bottom"),sQuery(id+"F24.wireOp",EDGE,"E84.top"),sQuery(id+"F24.wireOp",EDGE,"E84.left"),sQuery(id+"F24.wireOp",EDGE,"E84.right"),sQuery(id+"F24.wireOp",EDGE,"2IplUNgi-tkBv-9E8a-ZFnB-auiuJyXHGnih"),sQuery(id+"F24.wireOp",EDGE,"E85.left"),sQuery(id+"F24.wireOp",EDGE,"E85.right"),sQuery(id+"F24.wireOp",EDGE,"E86.trimOffspring"),sQuery(id+"F24.wireOp",EDGE,"dbc6eed9-552c-4b0d-aad6-60334d5a8f2e0.MirrorCS"),sQuery(id+"F24.wireOp",EDGE,"E99.MirrorCS"),sQuery(id+"F24.wireOp",EDGE,"E87.MirrorCS"),sQuery(id+"F24.wireOp",EDGE,"1bd0f054-9f5b-46f9-b1dd-c3be90d0bcb60.MirrorCS"),sQuery(id+"F24.wireOp",EDGE,"E88.MirrorCS"),sQuery(id+"F24.wireOp",EDGE,"E89.MirrorCS"),sQuery(id+"F24.wireOp",EDGE,"f50dec66-58dc-4cda-8118-78d90768280c0.MirrorCS"),sQuery(id+"F24.wireOp",EDGE,"E90.MirrorCS"),sQuery(id+"F24.wireOp",EDGE,"E91.MirrorCS")])],"isStart":false});
            var sketch = newSketch(context, id + "F31", { "sketchPlane" : qUnion([Q0])});
            skLineSegment(sketch, "E113.bottom", {"start": v(23.05, 8.5) * mm, "end": v(-27.5, 8.5) * mm});
            skLineSegment(sketch, "E113.top", {"start": v(23.05, -8.5) * mm, "end": v(-27.5, -8.5) * mm});
            skLineSegment(sketch, "E113.left", {"start": v(23.05, 8.5) * mm, "end": v(23.05, -8.5) * mm});
            skLineSegment(sketch, "E113.right", {"start": v(-27.5, 8.5) * mm, "end": v(-27.5, -8.5) * mm});
            skSolve(sketch);
        }
        {
            var Q0;
            Q0 = qSketchRegion(id + "F31", true);
            extrude(context, id + "F32", {"entities" : qUnion([Q0]), "operationType" : NewBodyOperationType.INTERSECT, "depth" : -50 * mm, "offsetDistance" : 25 * mm});
        }
        {
            var Q0;
            {var subQ0=sQuery(id+"F24.wireOp",EDGE,"E85.left");Q0=makeQuery(id+"F24.imprint","IMPRINT",FACE,{"disambiguationData":[TD([[makeQuery(id+"F24.imprint","IMPRINT",EDGE,{"derivedFrom":subQ0}),-1.0]])]});}
            var Q1;
            {var subQ0=sQuery(id+"F24.wireOp",EDGE,"E85.right");Q1=makeQuery(id+"F24.imprint","IMPRINT",FACE,{"disambiguationData":[TD([[makeQuery(id+"F24.imprint","IMPRINT",EDGE,{"derivedFrom":subQ0}),1.0]])]});}
            var Q2;
            {var subQ0=sQuery(id+"F24.wireOp",EDGE,"E87.MirrorCS");Q2=makeQuery(id+"F24.imprint","IMPRINT",FACE,{"disambiguationData":[TD([[makeQuery(id+"F24.imprint","IMPRINT",EDGE,{"derivedFrom":subQ0}),-1.0]])]});}
            var Q3;
            {var subQ0=sQuery(id+"F24.wireOp",EDGE,"E104");Q3=makeQuery(id+"F24.imprint","IMPRINT",FACE,{"disambiguationData":[TD([[makeQuery(id+"F24.imprint","IMPRINT",EDGE,{"derivedFrom":subQ0}),-1.0]])]});}
            var Q4;
            {var subQ0=sQuery(id+"F24.wireOp",EDGE,"E90.MirrorCS");Q4=makeQuery(id+"F24.imprint","IMPRINT",FACE,{"disambiguationData":[TD([[makeQuery(id+"F24.imprint","IMPRINT",EDGE,{"derivedFrom":subQ0}),1.0]])]});}
            var Q5;
            {var subQ0=sQuery(id+"F24.wireOp",EDGE,"E91.MirrorCS");Q5=makeQuery(id+"F24.imprint","IMPRINT",FACE,{"disambiguationData":[TD([[makeQuery(id+"F24.imprint","IMPRINT",EDGE,{"derivedFrom":subQ0}),-1.0]])]});}
            var Q6;
            {var subQ0=sQuery(id+"F24.wireOp",EDGE,"E89.MirrorCS");Q6=makeQuery(id+"F24.imprint","IMPRINT",FACE,{"disambiguationData":[TD([[makeQuery(id+"F24.imprint","IMPRINT",EDGE,{"derivedFrom":subQ0}),1.0]])]});}
            var Q7;
            {var subQ0=sQuery(id+"F24.wireOp",EDGE,"E88.MirrorCS");Q7=makeQuery(id+"F24.imprint","IMPRINT",FACE,{"disambiguationData":[TD([[makeQuery(id+"F24.imprint","IMPRINT",EDGE,{"derivedFrom":subQ0}),-1.0]])]});}
            extrude(context, id + "F33", {"entities" : qUnion([Q0, Q1, Q2, Q3, Q4, Q5, Q6, Q7]), "operationType" : NewBodyOperationType.ADD, "depth" : 2.5 * mm, "offsetDistance" : 25 * mm});
        }
    });
